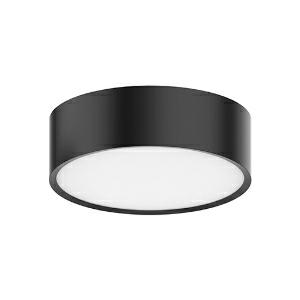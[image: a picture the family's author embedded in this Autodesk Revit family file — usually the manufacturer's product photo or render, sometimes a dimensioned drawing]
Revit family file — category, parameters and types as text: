
# Revit family: ledceilinglu-e_rd142-18w-840-bl_540001296000
name_source: partatom
category: Leuchten
revit_build: Autodesk Revit 2016 (Build: 20190508_0715(x64)
units: mm (PartAtom-declared; Revit-internal decimal feet)

## family parameters
Basisbauteil = Fläche
Beim Laden mit Abzugskörper schneiden = Nein
Bemaßung runder Anschluss = Durchmesser verwenden
Gemeinsam genutzt = Nein
Lichtquelle = Nein
Raumberechnungspunkt = Nein
Teiletyp = Normal

## types (1)
- LEDCeilingLu-E Rd142-18W-840-BL (1 x LED, 1710 lm)
    Approval mark = CE
    Beschreibung = Stylish and compact ceiling luminaire. Clean “twist-and-lock” mounting system. High quality full metal body. Low height of only 46mm. Suitable for ceiling and wall mounting.
    CIE Flux Codes = 49 79 96 100 100
    Control Gear = Electronic ballast
    Height = 100 mm  [stored 0.328084 ft]
    Hersteller = OPPLE
    Lamp Light Flux = 1710 lm
    Lamp count = 1
    Lampe = 1 x LED
    Length = 100 mm  [stored 0.328084 ft]
    Luminous efficacy = 95 lm/W
    ModVariant = Nein
    Modell = 540001296000
    Mounting Place = Wall, Ceiling
    Mounting Type = Surface mounted
    Number of Poles = 1
    OnlyDefault = Ja
    Power Factor = 1
    Product Name = LEDCeilingLu-E Rd142-18W-840-BL
    Product group = Ceiling Light Luna
    ProductGroupID = 305
    Protection Class = Protection class II
    Protection Degree = IP 20
    RLX_Detail_Level = 1
    RlxData = <blob elided: 129705 chars, md5=f4fda6d2>
    Scheinlast = 18 VA
    Socket = socket
    Standby Power = 0 W
    System Light Flux = 1710 lm
    System Power = 18 W
    Typenbild = luna_bl_rd142.jpg
    Typenkommentare = Product without accessories
    URL = http://relux.com
    VarID = ---
    Voltage = 230 V
    Voltage Range = 220-240 V
    Vorgabe-Ansicht = 1800 mm
    Weight = 0.00 kg
    Width = 100 mm  [stored 0.328084 ft]

note: [stored X ft] marks values corroborated as IEEE doubles in the binary element streams (Revit-internal decimal feet)

## geometry (parser evidence)
native form markers: Blend x4, Sweep x11
no freeform markers — native parametric forms only
